# Revit family: JC KONTAKTER JCK211 FI
name_source: partatom
category: Specialty Equipment
units: mm (PartAtom-declared; Revit-internal decimal feet)

## family parameters
Cut with Voids When Loaded = No
Enable Cutting in Views = Yes
Host = Face
Maintain Annotation Orientation = Yes
Part Type = Normal
Room Calculation Point = No
Round Connector Dimension = Use Diameter
Shared = No

## types (1)
- JCK211
    CE asiakirja = https://jckontakter.se
    Default Elevation = 800 mm  [stored 2.62467 ft]
    Description = Tämä kyynärkytkin on valmistettu iskunkestävästä ABS-muovista. Siinä on kupera kosketuspinta, jossa on kosketusviivat, jotka osoittavat, missä painiketta tulee painaa. Tämä malli tarjoaa vahvan värikontrastin valkoisen kosketuspinnan ja valkoisen kehyksen kanssa. Suunniteltu ensisijaisesti sisäkäyttöön, mutta voidaan käyttää myös ulkona, koska se on varustettu kosteudenkestävällä mikrokytkimellä, jonka IP-luokka on 67.
    Kansi = ABS 750SW (Valkoinen)
    Kotelo = ABS 750SW (Valkoinen)
    Manufacturer = JC Kontakter
    Mikrokytkimien määrä = 1
    Mikrokytkin = Standar NO IP67
    Model = JCK211
    Nimellisestä nimellisvirrasta = 1mA/4 V DC
    Pienin nimellisvirta = 12V Resistiivinen 6A Induktiivinen L/R 5ms 6A, 24V Resistiivinen 6A Induktiivinen L/R 5ms 5A
    Tekniken tuotekortti = https://www.jckontakter.fi
    Tuotteen paino = 0.230 kg
    URL = https://www.jckontakter.fi
    Valmistusmaa = Ruotsi

note: [stored X ft] marks values corroborated as IEEE doubles in the binary element streams (Revit-internal decimal feet)

## geometry (parser evidence)
native form markers: Sweep x5
no freeform markers — native parametric forms only
